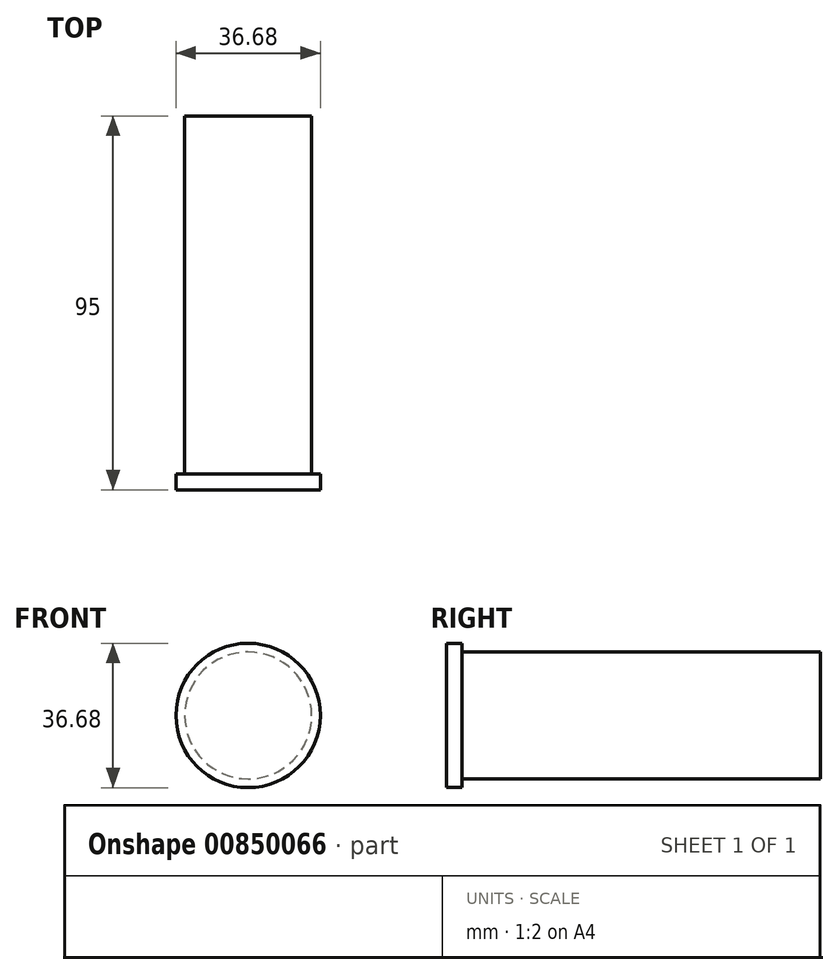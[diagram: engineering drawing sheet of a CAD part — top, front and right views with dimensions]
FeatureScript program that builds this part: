
annotation { "Feature Type Name" : "Feature", "Feature Type Description" : "" }
export const myFeature = defineFeature(function(context is Context, id is Id, definition is map)
    precondition{}
    {
        {
            var Q0;
            Q0=qCreatedBy(makeId("Front.planeOp"),FACE);
            var sketch = newSketch(context, id + "F0", { "sketchPlane" : qUnion([Q0])});
            skCircle(sketch, "E0", {"center": v(0, 0) * mm, "radius": 18.34 * mm});
            skSolve(sketch);
        }
        {
            var Q0;
            Q0 = qSketchRegion(id + "F0", true);
            extrude(context, id + "F1", {"entities" : qUnion([Q0]), "depth" : 4 * mm, "offsetDistance" : 25.4 * mm});
        }
        {
            var Q0;
            Q0=makeQuery(id+"F1.opExtrude","CAP_FACE",FACE,{"disambiguationData":[OSD([sQuery(id+"F0.wireOp",EDGE,"E0")])],"isStart":true});
            var sketch = newSketch(context, id + "F2", { "sketchPlane" : qUnion([Q0])});
            skCircle(sketch, "E1", {"center": v(0, 0) * mm, "radius": 16.12 * mm});
            skSolve(sketch);
        }
        {
            var Q0;
            Q0=makeQuery(id+"F2.imprint","IMPRINT",FACE,{"disambiguationData":[TD([[makeQuery(id+"F2.imprint","IMPRINT",EDGE,{"derivedFrom":sQuery(id+"F2.wireOp",EDGE,"E1")}),1.0]])]});
            extrude(context, id + "F3", {"entities" : qUnion([Q0]), "operationType" : NewBodyOperationType.ADD, "depth" : 91 * mm, "offsetDistance" : 25.4 * mm});
        }
    });
